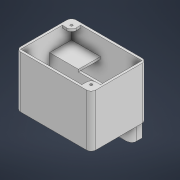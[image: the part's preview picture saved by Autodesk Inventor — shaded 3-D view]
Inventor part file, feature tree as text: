
AUTODESK INVENTOR PART (.ipt)
format: ipt  version: 2022 (Build 260153000, 153)  size: 220,672 bytes
history: native  units: in
note: dims shown in document units (in); Inventor stores cm internally (conversion verified against a paired STEP export)
features: extrude x11, sketch x11, fillet x8, shell x1
ambient origin geometry x8: Origin, YZ Plane, XZ Plane, XY Plane, X Axis, Y Axis, Z Axis, Center Point
bodies: Solid1 (feature_tree)
feature tree (31):
  extrude  "Extrusion1"  Depth=1.7717in
  shell  "Shell1"  Thickness=1.8898in
  extrude  "Extrusion2"  Depth=1.1811in
  extrude  "Extrusion3"  Depth=2.4016in
  fillet  "Fillet1"  [1 undecoded]
  fillet  "Fillet2"  Radius=1.7323in
  fillet  "Fillet3"  Radius=0.0787in
  fillet  "Fillet4"  Radius=1.0236in
  extrude  "Extrusion4"  Depth=0.1575in
  extrude  "Extrusion5"  Depth=0.1575in
  extrude  "Extrusion7"  Depth=0.9843in TaperAngle=0.0deg
  fillet  "Fillet6"  Radius=0.3937in
  extrude  "Extrusion10"  Depth=0.0787in
  extrude  "Extrusion11"  Depth=0.0787in TaperAngle=0.0deg
  fillet  "Fillet7"  Radius=0.1575in
  extrude  "Extrusion12"  Depth=0.0787in
  fillet  "Fillet8"  Radius=0.315in
  extrude  "Extrusion13"  Depth=0.1575in
  fillet  "Fillet9"  Radius=0.5906in
  extrude  "Extrusion14"  Depth=0.5906in TaperAngle=0.0deg
  sketch  "Sketch1"  dims[d3=2.5591in d4=1.7717in d5=1.8898in d6=0.0in]
  sketch  "Sketch2"  dims[d7=0.0787in d9=1.1811in]
  sketch  "Sketch3"  dims[d10=0.3937in d11=2.4016in d12=0.0in d13=0.0in d16=1.7323in d17=0.0787in d18=1.0236in d19=0.0in]
  sketch  "Sketch4"  dims[d20=0.1575in d21=0.1575in]
  sketch  "Sketch8"  dims[d22=0.1575in d23=0.1575in]
  sketch  "Sketch10"  dims[d24=0.0787in d25=0.9843in d26=0.0in d27=0.3937in]
  sketch  "Sketch13"  dims[d28=0.315in d29=0.0787in]
  sketch  "Sketch14"  dims[d30=0.315in d31=0.0in d38=0.0787in d39=0.0in d50=0.1575in]
  sketch  "Sketch15"  dims[d51=0.315in d52=0.0787in d53=0.315in d54=0.0in]
  sketch  "Sketch16"  dims[d58=0.0787in d59=0.0in d60=0.1575in d62=0.5906in d63=0.0in]
  sketch  "Sketch17"  dims[d64=0.3937in d68=0.5906in d69=0.0in d70=0.2756in d74=0.0in d75=0.0in d65=0.0in d66=0.0in d67=0.0in d71=0.0394in d72=0.0394in d73=0.0059in d76=0.5635in d77=0.0295in d78=0.8108in d79=0.0025in d80=0.0295in d81=0.0148in]
note: 1 required parameter value undecoded (feature->parameter linkage not recoverable at this tier; creation-order binding heuristic only, values carry confidence <= 0.55)
